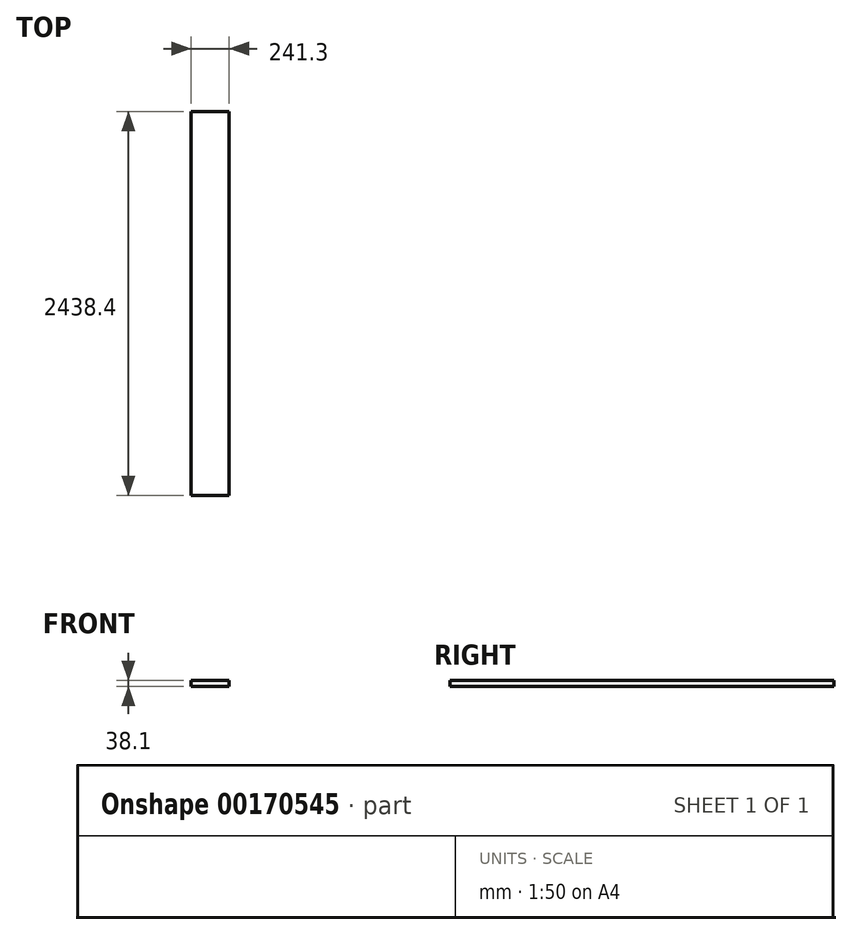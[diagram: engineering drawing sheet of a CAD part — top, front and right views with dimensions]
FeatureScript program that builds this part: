
annotation { "Feature Type Name" : "Feature", "Feature Type Description" : "" }
export const myFeature = defineFeature(function(context is Context, id is Id, definition is map)
    precondition{}
    {
        {
            var Q0;
            Q0=qCreatedBy(makeId("Front.planeOp"),FACE);
            var sketch = newSketch(context, id + "F0", { "sketchPlane" : qUnion([Q0])});
            skLineSegment(sketch, "E0.bottom", {"start": v(-135.49, -77.58) * mm, "end": v(105.81, -77.58) * mm});
            skLineSegment(sketch, "E0.top", {"start": v(-135.49, -115.68) * mm, "end": v(105.81, -115.68) * mm});
            skLineSegment(sketch, "E0.left", {"start": v(-135.49, -77.58) * mm, "end": v(-135.49, -115.68) * mm});
            skLineSegment(sketch, "E0.right", {"start": v(105.81, -77.58) * mm, "end": v(105.81, -115.68) * mm});
            skSolve(sketch);
        }
        {
            var Q0;
            Q0=makeQuery(id+"F0.imprint","IMPRINT",FACE,{"disambiguationData":[TD([[makeQuery(id+"F0.imprint","IMPRINT",EDGE,{"derivedFrom":sQuery(id+"F0.wireOp",EDGE,"E0.bottom")}),-1.0]])]});
            extrude(context, id + "F1", {"entities" : qUnion([Q0]), "depth" : 2438.4 * mm});
        }
    });
